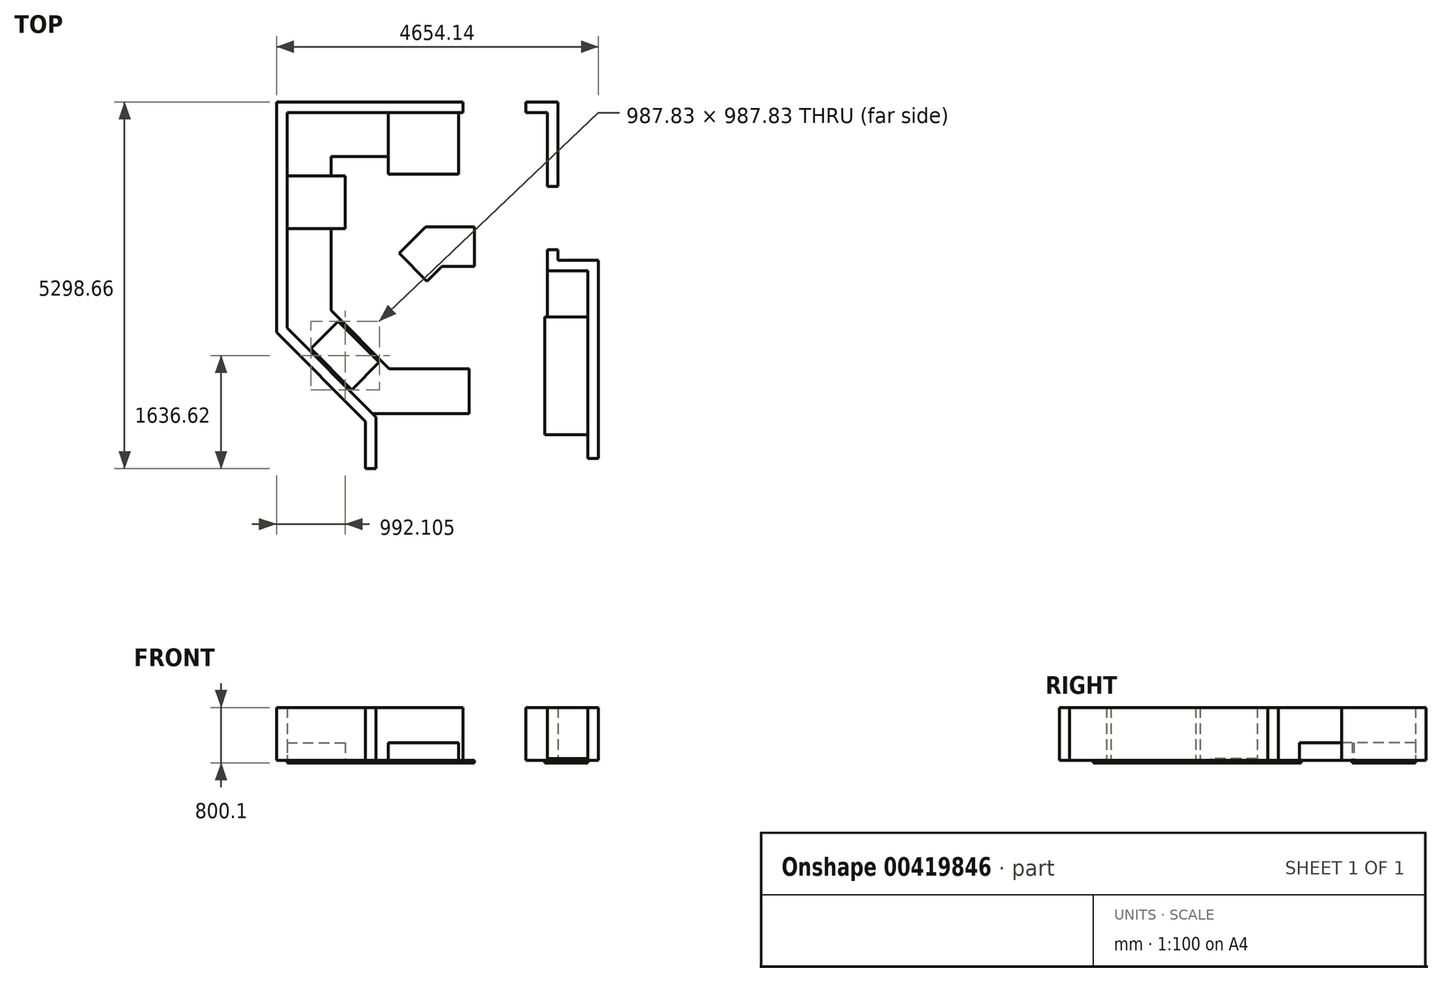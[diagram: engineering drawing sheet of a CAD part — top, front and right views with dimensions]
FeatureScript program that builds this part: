
annotation { "Feature Type Name" : "Feature", "Feature Type Description" : "" }
export const myFeature = defineFeature(function(context is Context, id is Id, definition is map)
    precondition{}
    {
        {
            var Q0;
            Q0=qCreatedBy(makeId("Top.planeOp"),FACE);
            var sketch = newSketch(context, id + "F0", { "sketchPlane" : qUnion([Q0])});
            skLineSegment(sketch, "E0", {"start": v(0, 0) * mm, "end": v(469.9, 0) * mm});
            skLineSegment(sketch, "E1", {"start": v(469.9, 0) * mm, "end": v(469.9, 571.5) * mm});
            skLineSegment(sketch, "E2", {"start": v(469.9, 571.5) * mm, "end": v(-236.72, 571.5) * mm});
            skLineSegment(sketch, "E3", {"start": v(-236.72, 571.5) * mm, "end": v(-619.64, 188.59) * mm});
            skLineSegment(sketch, "E4", {"start": v(-619.64, 188.59) * mm, "end": v(-215.53, -215.53) * mm});
            skLineSegment(sketch, "E5", {"start": v(-215.53, -215.53) * mm, "end": v(0, 0) * mm});
            skLineSegment(sketch, "E6.bottom", {"start": v(1485.9, -729.84) * mm, "end": v(2108.2, -729.84) * mm});
            skLineSegment(sketch, "E6.top", {"start": v(1485.9, -2431.64) * mm, "end": v(2108.2, -2431.64) * mm});
            skLineSegment(sketch, "E6.left", {"start": v(1485.9, -729.84) * mm, "end": v(1485.9, -2431.64) * mm});
            skLineSegment(sketch, "E6.right", {"start": v(2108.2, -729.84) * mm, "end": v(2108.2, -2431.64) * mm});
            skLineSegment(sketch, "E7.bottom", {"start": v(393.7, -2126.84) * mm, "end": v(-1003.3, -2126.84) * mm});
            skLineSegment(sketch, "E7.top", {"start": v(393.7, -1477.56) * mm, "end": v(-762, -1477.56) * mm});
            skLineSegment(sketch, "E7.left", {"start": v(393.7, -2126.84) * mm, "end": v(393.7, -1477.56) * mm});
            skLineSegment(sketch, "E8.left", {"start": v(-2241.14, -889) * mm, "end": v(-2241.14, 2222.5) * mm});
            skLineSegment(sketch, "E8.right", {"start": v(-1606.14, -633.41) * mm, "end": v(-1606.14, 1587.5) * mm});
            skLineSegment(sketch, "E9.bottom", {"start": v(-2241.14, 2222.5) * mm, "end": v(-780.64, 2222.5) * mm});
            skLineSegment(sketch, "E9.top", {"start": v(-1606.14, 1587.5) * mm, "end": v(-780.64, 1587.5) * mm});
            skLineSegment(sketch, "E9.right", {"start": v(-780.64, 2222.5) * mm, "end": v(-780.64, 1587.5) * mm});
            skLineSegment(sketch, "E10", {"start": v(-1606.14, -633.41) * mm, "end": v(-762, -1477.56) * mm});
            skLineSegment(sketch, "E11", {"start": v(-2241.14, -889) * mm, "end": v(-1003.3, -2126.84) * mm});
            skLineSegment(sketch, "E12", {"start": v(-1622.22, -1507.92) * mm, "end": v(-1184.07, -1069.77) * mm, "construction": true});
            skPoint(sketch, "E12.endSnap0", {"position": v(-1184.07, -1055.48) * mm});
            skLineSegment(sketch, "E13", {"start": v(-1500.22, -793.22) * mm, "end": v(-907.52, -1385.92) * mm});
            skLineSegment(sketch, "E14", {"start": v(-907.52, -1385.92) * mm, "end": v(-1302.65, -1781.05) * mm});
            skLineSegment(sketch, "E15", {"start": v(-1302.65, -1781.05) * mm, "end": v(-1895.35, -1188.35) * mm});
            skLineSegment(sketch, "E16", {"start": v(-1895.35, -1188.35) * mm, "end": v(-1500.22, -793.22) * mm});
            skLineSegment(sketch, "E17", {"start": v(-1697.78, -990.79) * mm, "end": v(-1105.09, -1583.48) * mm, "construction": true});
            skPoint(sketch, "E18", {"position": v(-1401.43, -1287.13) * mm});
            skLineSegment(sketch, "E19", {"start": v(-2241.14, 1308.1) * mm, "end": v(-1606.14, 1308.1) * mm});
            skLineSegment(sketch, "E20", {"start": v(-2241.14, 546.1) * mm, "end": v(-1606.14, 546.1) * mm});
            skSolve(sketch);
        }
        {
            var Q0;
            Q0=makeQuery(id+"F0.imprint","IMPRINT",FACE,{"disambiguationData":[TD([[makeQuery(id+"F0.imprint","IMPRINT",EDGE,{"derivedFrom":sQuery(id+"F0.wireOp",EDGE,"E0")}),1.0]])]});
            var Q1;
            Q1=makeQuery(id+"F0.imprint","IMPRINT",FACE,{"disambiguationData":[TD([[makeQuery(id+"F0.imprint","IMPRINT",EDGE,{"derivedFrom":sQuery(id+"F0.wireOp",EDGE,"E6.bottom")}),-1.0]])]});
            var Q2;
            {var subQ0=sQuery(id+"F0.wireOp",EDGE,"E9.bottom");Q2=makeQuery(id+"F0.imprint","IMPRINT",FACE,{"disambiguationData":[TD([[makeQuery(id+"F0.imprint","IMPRINT",EDGE,{"derivedFrom":subQ0}),-1.0]])]});}
            var Q3;
            Q3=makeQuery(id+"F0.imprint","IMPRINT",FACE,{"disambiguationData":[TD([[makeQuery(id+"F0.imprint","IMPRINT",EDGE,{"derivedFrom":sQuery(id+"F0.wireOp",EDGE,"E7.bottom")}),-1.0]])]});
            extrude(context, id + "F1", {"entities" : qUnion([Q0, Q1, Q2, Q3]), "depth" : 38.1 * mm});
        }
        {
            var Q0;
            Q0=makeQuery(id+"F1.opExtrude","CAP_FACE",FACE,{"disambiguationData":[OSD([sQuery(id+"F0.wireOp",EDGE,"E7.bottom"),sQuery(id+"F0.wireOp",EDGE,"E7.top"),sQuery(id+"F0.wireOp",EDGE,"E7.left"),sQuery(id+"F0.wireOp",EDGE,"E8.left"),sQuery(id+"F0.wireOp",EDGE,"E8.right"),sQuery(id+"F0.wireOp",EDGE,"E10"),sQuery(id+"F0.wireOp",EDGE,"E11"),sQuery(id+"F0.wireOp",EDGE,"E20")])],"isStart":false});
            var sketch = newSketch(context, id + "F2", { "sketchPlane" : qUnion([Q0])});
            skLineSegment(sketch, "E21.0", {"start": v(-2241.14, 1308.1) * mm, "end": v(-1606.14, 1308.1) * mm});
            skLineSegment(sketch, "E22.0", {"start": v(-2241.14, 546.1) * mm, "end": v(-1606.14, 546.1) * mm});
            skLineSegment(sketch, "E23", {"start": v(-2241.14, 1308.1) * mm, "end": v(-2241.14, 546.1) * mm});
            skLineSegment(sketch, "E24", {"start": v(-1402.94, 1308.1) * mm, "end": v(-1402.94, 546.1) * mm});
            skLineSegment(sketch, "E25", {"start": v(-1402.94, 546.1) * mm, "end": v(-1606.14, 546.1) * mm});
            skLineSegment(sketch, "E26", {"start": v(-1402.94, 1308.1) * mm, "end": v(-1606.14, 1308.1) * mm});
            skLineSegment(sketch, "E27.0", {"start": v(-780.64, 2222.5) * mm, "end": v(-780.64, 1587.5) * mm});
            skLineSegment(sketch, "E28", {"start": v(-780.64, 1587.5) * mm, "end": v(-780.64, 1333.5) * mm});
            skLineSegment(sketch, "E29", {"start": v(-780.64, 1333.5) * mm, "end": v(235.36, 1333.5) * mm});
            skLineSegment(sketch, "E30", {"start": v(235.36, 1333.5) * mm, "end": v(235.36, 2222.5) * mm});
            skLineSegment(sketch, "E31", {"start": v(235.36, 2222.5) * mm, "end": v(-780.64, 2222.5) * mm});
            skSolve(sketch);
        }
        {
            var Q0;
            Q0=makeQuery(id+"F2.imprint","IMPRINT",FACE,{"disambiguationData":[TD([[makeQuery(id+"F2.imprint","IMPRINT",EDGE,{"derivedFrom":sQuery(id+"F2.wireOp",EDGE,"E27.0")}),1.0]])]});
            var Q1;
            Q1=makeQuery(id+"F2.imprint","IMPRINT",FACE,{"disambiguationData":[TD([[makeQuery(id+"F2.imprint","IMPRINT",EDGE,{"derivedFrom":sQuery(id+"F2.wireOp",EDGE,"E21.0")}),-1.0]])]});
            extrude(context, id + "F3", {"entities" : qUnion([Q0, Q1]), "depth" : 254 * mm});
        }
        {
            var Q0;
            Q0=makeQuery(id+"F1.opExtrude","CAP_FACE",FACE,{"disambiguationData":[OSD([sQuery(id+"F0.wireOp",EDGE,"E8.left"),sQuery(id+"F0.wireOp",EDGE,"E8.right"),sQuery(id+"F0.wireOp",EDGE,"E9.bottom"),sQuery(id+"F0.wireOp",EDGE,"E9.top"),sQuery(id+"F0.wireOp",EDGE,"E9.right"),sQuery(id+"F0.wireOp",EDGE,"E19")])],"isStart":false});
            var sketch = newSketch(context, id + "F4", { "sketchPlane" : qUnion([Q0])});
            skLineSegment(sketch, "E32", {"start": v(-2241.14, 2222.5) * mm, "end": v(298.86, 2222.5) * mm});
            skLineSegment(sketch, "E33", {"start": v(298.86, 2222.5) * mm, "end": v(298.86, 2374.9) * mm});
            skLineSegment(sketch, "E34", {"start": v(298.86, 2374.9) * mm, "end": v(-2393.54, 2374.9) * mm});
            skLineSegment(sketch, "E35", {"start": v(-2393.54, 2374.9) * mm, "end": v(-2393.54, -952.13) * mm});
            skLineSegment(sketch, "E36", {"start": v(-2393.54, -952.13) * mm, "end": v(-1104.9, -2240.77) * mm});
            skLineSegment(sketch, "E37", {"start": v(-1104.9, -2240.77) * mm, "end": v(-1104.9, -2923.76) * mm});
            skLineSegment(sketch, "E38", {"start": v(-1104.9, -2923.76) * mm, "end": v(-952.5, -2923.76) * mm});
            skLineSegment(sketch, "E39", {"start": v(-952.5, -2923.76) * mm, "end": v(-952.5, -2177.64) * mm});
            skLineSegment(sketch, "E40.0", {"start": v(-2241.14, -889) * mm, "end": v(-2241.14, 546.1) * mm});
            skLineSegment(sketch, "E40.1", {"start": v(-2241.14, -889) * mm, "end": v(-952.5, -2177.64) * mm});
            skPoint(sketch, "E41.orphan", {"position": v(-1003.3, -2126.84) * mm});
            skLineSegment(sketch, "E42.0", {"start": v(2108.2, -425.04) * mm, "end": v(2108.2, -2776) * mm});
            skLineSegment(sketch, "E43", {"start": v(2260.6, 88.9) * mm, "end": v(2260.6, -2776) * mm});
            skLineSegment(sketch, "E44", {"start": v(2260.6, -2776) * mm, "end": v(2108.2, -2776) * mm});
            skPoint(sketch, "E45.orphan", {"position": v(2108.2, -729.84) * mm});
            skPoint(sketch, "E46.orphan", {"position": v(2108.2, -2431.64) * mm});
            skLineSegment(sketch, "E47", {"start": v(-2241.14, 2222.5) * mm, "end": v(-2241.14, -889) * mm});
            skLineSegment(sketch, "E48", {"start": v(1213.26, 2374.9) * mm, "end": v(1670.46, 2374.9) * mm});
            skLineSegment(sketch, "E49", {"start": v(1670.46, 2374.9) * mm, "end": v(1670.46, 1155.7) * mm});
            skLineSegment(sketch, "E50", {"start": v(1670.46, 1155.7) * mm, "end": v(1518.06, 1155.7) * mm});
            skLineSegment(sketch, "E51", {"start": v(1518.06, 1155.7) * mm, "end": v(1518.06, 2222.5) * mm});
            skLineSegment(sketch, "E52", {"start": v(1518.06, 2222.5) * mm, "end": v(1213.26, 2222.5) * mm});
            skLineSegment(sketch, "E53", {"start": v(1213.26, 2222.5) * mm, "end": v(1213.26, 2374.9) * mm});
            skLineSegment(sketch, "E54", {"start": v(1518.06, 241.3) * mm, "end": v(1670.46, 241.3) * mm});
            skLineSegment(sketch, "E55", {"start": v(1670.46, 241.3) * mm, "end": v(1670.46, 88.9) * mm});
            skLineSegment(sketch, "E56", {"start": v(1670.46, 88.9) * mm, "end": v(2260.6, 88.9) * mm});
            skLineSegment(sketch, "E57", {"start": v(1518.06, 241.3) * mm, "end": v(1518.06, -63.5) * mm});
            skLineSegment(sketch, "E58", {"start": v(1518.06, -63.5) * mm, "end": v(2108.2, -63.5) * mm});
            skLineSegment(sketch, "E59", {"start": v(2108.2, -63.5) * mm, "end": v(2108.2, -425.04) * mm});
            skPoint(sketch, "E60.orphan", {"position": v(2260.6, -425.04) * mm});
            skLineSegment(sketch, "E61", {"start": v(1518.06, -63.5) * mm, "end": v(1518.06, -729.84) * mm});
            skPoint(sketch, "E62.0", {"position": v(1797.05, -729.84) * mm});
            skLineSegment(sketch, "E63.0", {"start": v(1518.06, -729.84) * mm, "end": v(2108.2, -729.84) * mm});
            skPoint(sketch, "E64.orphan", {"position": v(1485.9, -729.84) * mm});
            skSolve(sketch);
        }
        {
            var Q0;
            {var subQ5=sQuery(id+"F4.wireOp",EDGE,"E33");Q0=makeQuery(id+"F4.imprint","IMPRINT",FACE,{"disambiguationData":[TD([[makeQuery(id+"F4.imprint","IMPRINT",EDGE,{"derivedFrom":subQ5}),1.0]])]});}
            var Q1;
            Q1=makeQuery(id+"F4.imprint","IMPRINT",FACE,{"disambiguationData":[TD([[makeQuery(id+"F4.imprint","IMPRINT",EDGE,{"derivedFrom":sQuery(id+"F4.wireOp",EDGE,"E42.0")}),1.0]])]});
            var Q2;
            Q2=makeQuery(id+"F4.imprint","IMPRINT",FACE,{"disambiguationData":[TD([[makeQuery(id+"F4.imprint","IMPRINT",EDGE,{"derivedFrom":sQuery(id+"F4.wireOp",EDGE,"E48")}),-1.0]])]});
            extrude(context, id + "F5", {"entities" : qUnion([Q0, Q1, Q2]), "depth" : 762 * mm});
        }
        {
            var Q0;
            Q0=makeQuery(id+"F4.imprint","IMPRINT",FACE,{"disambiguationData":[TD([[makeQuery(id+"F4.imprint","IMPRINT",EDGE,{"derivedFrom":sQuery(id+"F4.wireOp",EDGE,"E58")}),-1.0]])]});
            extrude(context, id + "F6", {"entities" : qUnion([Q0]), "operationType" : NewBodyOperationType.ADD, "depth" : 25.4 * mm});
        }
    });
